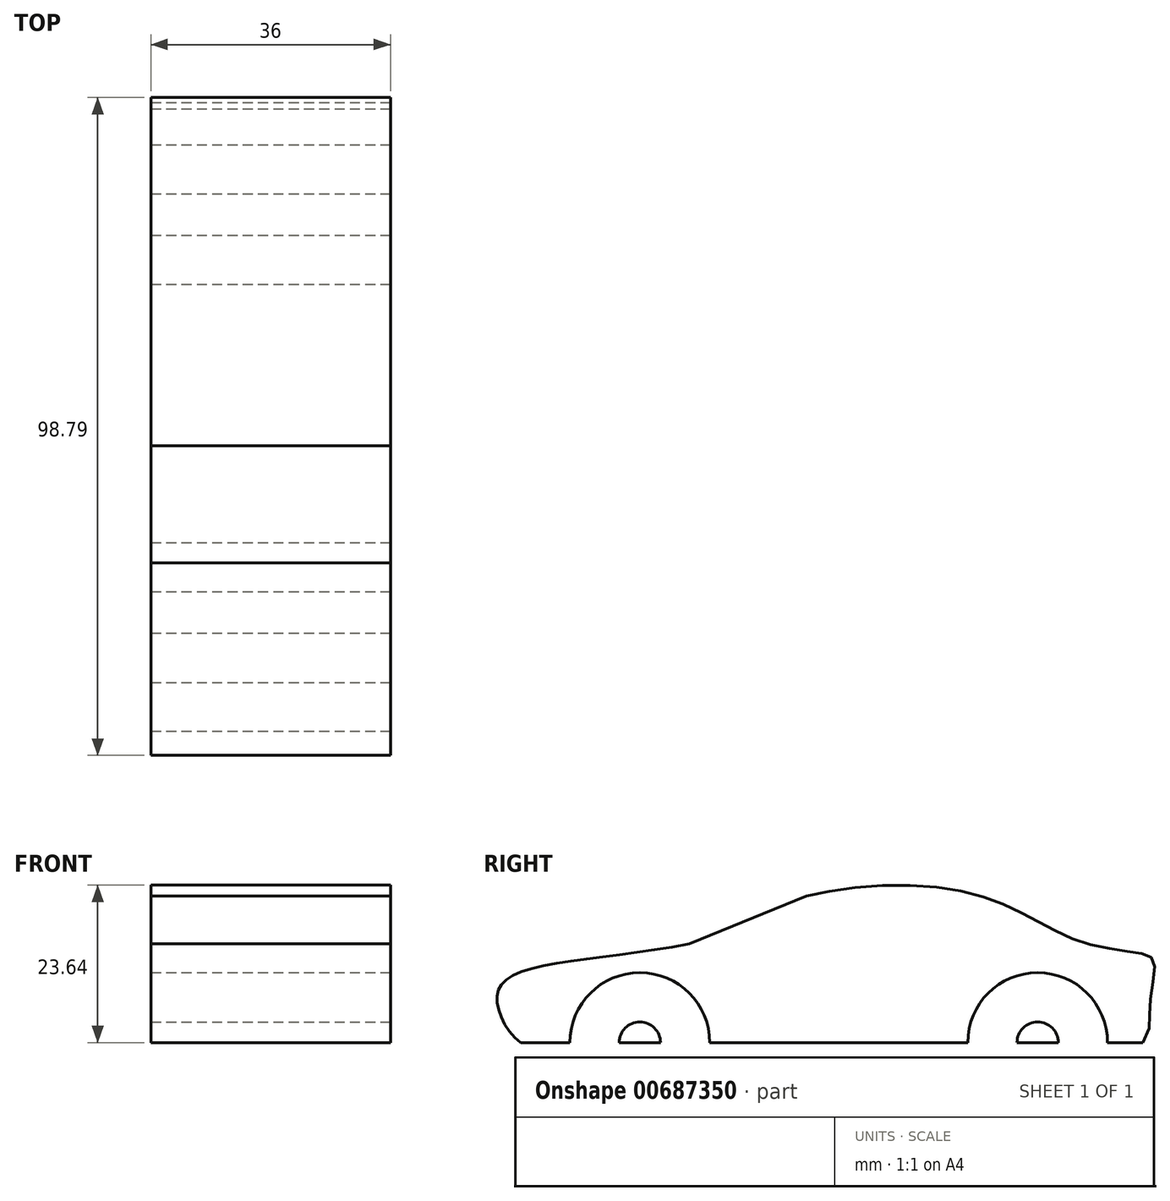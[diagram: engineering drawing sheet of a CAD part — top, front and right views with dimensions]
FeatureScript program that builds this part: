
annotation { "Feature Type Name" : "Feature", "Feature Type Description" : "" }
export const myFeature = defineFeature(function(context is Context, id is Id, definition is map)
    precondition{}
    {
        {
            var Q0;
            Q0=qCreatedBy(makeId("Right.planeOp"),FACE);
            var sketch = newSketch(context, id + "F0", { "sketchPlane" : qUnion([Q0])});
            skFitSpline(sketch, "E0", {"points": [v(0, 0) * mm, v(-17.92, 0) * mm], "startDerivative": vector(-17.92, 0) * mm, "endDerivative": vector(-17.92, 0) * mm});
            skFitSpline(sketch, "E1", {"points": [v(-17.92, 0) * mm, v(-21.44, 6.1) * mm, v(-19, 10.12) * mm, v(7.46, 14.82) * mm], "startDerivative": vector(-21.25, 15.42) * mm, "endDerivative": vector(59.63, 11.91) * mm});
            skLineSegment(sketch, "E2", {"start": v(7.46, 14.82) * mm, "end": v(25.02, 21.98) * mm});
            skFitSpline(sketch, "E3", {"points": [v(25.02, 21.98) * mm, v(43.8, 23.44) * mm, v(57.12, 19.62) * mm, v(66.03, 15.23) * mm, v(74.85, 13.45) * mm, v(77.2, 12.27) * mm, v(76.61, 5.61) * mm, v(75.56, 0) * mm], "startDerivative": vector(72.38, 18.5) * mm, "endDerivative": vector(-38.34, -51.68) * mm});
            skLineSegment(sketch, "E4", {"start": v(75.56, 0) * mm, "end": v(-5.97, 0) * mm});
            skSolve(sketch);
        }
        {
            var Q0;
            Q0 = qSketchRegion(id + "F0", true);
            extrude(context, id + "F1", {"entities" : qUnion([Q0]), "endBound" : BoundingType.SYMMETRIC, "depth" : 18 * 2 * mm, "offsetDistance" : 25 * mm});
        }
        {
            var Q0;
            Q0=makeQuery(id+"F1.opExtrude","CAP_FACE",FACE,{"disambiguationData":[OSD([sQuery(id+"F0.wireOp",EDGE,"E0"),sQuery(id+"F0.wireOp",EDGE,"E1"),sQuery(id+"F0.wireOp",EDGE,"E2"),sQuery(id+"F0.wireOp",EDGE,"E3"),sQuery(id+"F0.wireOp",EDGE,"E4")])],"isStart":false});
            var sketch = newSketch(context, id + "F2", { "sketchPlane" : qUnion([Q0])});
            skCircle(sketch, "E5", {"center": v(0, 0) * mm, "radius": 10.5 * mm});
            skLineSegment(sketch, "E6.bottom", {"start": v(0, -4.82) * mm, "end": v(5, -4.82) * mm});
            skLineSegment(sketch, "E6.top", {"start": v(0, 12.37) * mm, "end": v(5, 12.37) * mm});
            skLineSegment(sketch, "E6.left", {"start": v(0, -4.82) * mm, "end": v(0, 12.37) * mm});
            skLineSegment(sketch, "E6.right", {"start": v(5, -4.82) * mm, "end": v(5, 12.37) * mm});
            skLineSegment(sketch, "E7.MirrorCS", {"start": v(0, -4.82) * mm, "end": v(-5, -4.82) * mm});
            skLineSegment(sketch, "E8.MirrorCS", {"start": v(0, 12.37) * mm, "end": v(-5, 12.37) * mm});
            skLineSegment(sketch, "E9.MirrorCS", {"start": v(-5, -4.82) * mm, "end": v(-5, 12.37) * mm});
            skCircle(sketch, "E10", {"center": v(0, 0) * mm, "radius": 3.1 * mm});
            skCircle(sketch, "E11", {"center": v(59.77, 0) * mm, "radius": 10.5 * mm});
            skLineSegment(sketch, "E12.bottom", {"start": v(59.77, -4.82) * mm, "end": v(64.77, -4.82) * mm});
            skLineSegment(sketch, "E12.top", {"start": v(59.77, 12.37) * mm, "end": v(64.77, 12.37) * mm});
            skLineSegment(sketch, "E12.left", {"start": v(59.77, -4.82) * mm, "end": v(59.77, 12.37) * mm});
            skLineSegment(sketch, "E12.right", {"start": v(64.77, -4.82) * mm, "end": v(64.77, 12.37) * mm});
            skLineSegment(sketch, "E13.MirrorCS", {"start": v(59.77, -4.82) * mm, "end": v(54.77, -4.82) * mm});
            skLineSegment(sketch, "E14.MirrorCS", {"start": v(59.77, 12.37) * mm, "end": v(54.77, 12.37) * mm});
            skLineSegment(sketch, "E15.MirrorCS", {"start": v(54.77, -4.82) * mm, "end": v(54.77, 12.37) * mm});
            skCircle(sketch, "E16", {"center": v(59.77, 0) * mm, "radius": 3.1 * mm});
            skSolve(sketch);
        }
        {
            var Q0;
            {var subQ0=sQuery(id+"F2.wireOp",EDGE,"E7.MirrorCS");Q0=makeQuery(id+"F2.imprint","IMPRINT",FACE,{"disambiguationData":[TD([[makeQuery(id+"F2.imprint","IMPRINT",EDGE,{"derivedFrom":subQ0}),-1.0]])]});}
            var Q1;
            {var subQ6=sQuery(id+"F2.wireOp",EDGE,"E6.bottom");Q1=makeQuery(id+"F2.imprint","IMPRINT",FACE,{"disambiguationData":[TD([[makeQuery(id+"F2.imprint","IMPRINT",EDGE,{"derivedFrom":subQ6}),1.0]])]});}
            var Q2;
            {var subQ0=sQuery(id+"F2.wireOp",EDGE,"E13.MirrorCS");Q2=makeQuery(id+"F2.imprint","IMPRINT",FACE,{"disambiguationData":[TD([[makeQuery(id+"F2.imprint","IMPRINT",EDGE,{"derivedFrom":subQ0}),-1.0]])]});}
            var Q3;
            {var subQ6=sQuery(id+"F2.wireOp",EDGE,"E12.bottom");Q3=makeQuery(id+"F2.imprint","IMPRINT",FACE,{"disambiguationData":[TD([[makeQuery(id+"F2.imprint","IMPRINT",EDGE,{"derivedFrom":subQ6}),1.0]])]});}
            var Q4;
            Q4=makeQuery(id+"F1.opExtrude","CAP_FACE",FACE,{"disambiguationData":[OSD([sQuery(id+"F0.wireOp",EDGE,"E0"),sQuery(id+"F0.wireOp",EDGE,"E1"),sQuery(id+"F0.wireOp",EDGE,"E2"),sQuery(id+"F0.wireOp",EDGE,"E3"),sQuery(id+"F0.wireOp",EDGE,"E4")])],"isStart":true});
            extrude(context, id + "F3", {"entities" : qUnion([Q0, Q1, Q2, Q3]), "operationType" : NewBodyOperationType.ADD, "endBound" : BoundingType.UP_TO_SURFACE, "oppositeDirection" : true, "depth" : 25 * mm, "endBoundEntityFace" : qUnion([Q4]), "offsetDistance" : 25 * mm});
        }
        {
            var Q0;
            {var subQ0=sQuery(id+"F2.wireOp",EDGE,"E9.MirrorCS");var subQ1=sQuery(id+"F2.wireOp",EDGE,"E5");var subQ2=makeQuery(id+"F2.imprint","INTERSECT",VERTEX,{"derivedFrom":[subQ1,subQ0]});Q0=makeQuery(id+"F2.imprint","IMPRINT",FACE,{"disambiguationData":[TD([[makeQuery(id+"F2.imprint","IMPRINT",EDGE,{"disambiguationData":[TD([[subQ2,-1.0]])],"derivedFrom":subQ1}),1.0]])]});}
            var Q1;
            {var subQ0=sQuery(id+"F2.wireOp",EDGE,"E6.right");var subQ1=sQuery(id+"F2.wireOp",EDGE,"E5");var subQ2=makeQuery(id+"F2.imprint","INTERSECT",VERTEX,{"derivedFrom":[subQ1,subQ0]});Q1=makeQuery(id+"F2.imprint","IMPRINT",FACE,{"disambiguationData":[TD([[makeQuery(id+"F2.imprint","IMPRINT",EDGE,{"disambiguationData":[TD([[subQ2,1.0]])],"derivedFrom":subQ1}),1.0]])]});}
            var Q2;
            {var subQ0=sQuery(id+"F2.wireOp",EDGE,"E15.MirrorCS");var subQ1=sQuery(id+"F2.wireOp",EDGE,"E11");var subQ2=makeQuery(id+"F2.imprint","INTERSECT",VERTEX,{"derivedFrom":[subQ1,subQ0]});Q2=makeQuery(id+"F2.imprint","IMPRINT",FACE,{"disambiguationData":[TD([[makeQuery(id+"F2.imprint","IMPRINT",EDGE,{"disambiguationData":[TD([[subQ2,-1.0]])],"derivedFrom":subQ1}),1.0]])]});}
            var Q3;
            {var subQ0=sQuery(id+"F2.wireOp",EDGE,"E12.right");var subQ1=sQuery(id+"F2.wireOp",EDGE,"E11");var subQ2=makeQuery(id+"F2.imprint","INTERSECT",VERTEX,{"derivedFrom":[subQ1,subQ0]});Q3=makeQuery(id+"F2.imprint","IMPRINT",FACE,{"disambiguationData":[TD([[makeQuery(id+"F2.imprint","IMPRINT",EDGE,{"disambiguationData":[TD([[subQ2,1.0]])],"derivedFrom":subQ1}),1.0]])]});}
            extrude(context, id + "F4", {"entities" : qUnion([Q0, Q1, Q2, Q3]), "operationType" : NewBodyOperationType.REMOVE, "endBound" : BoundingType.THROUGH_ALL, "oppositeDirection" : true, "depth" : 25 * mm, "offsetDistance" : 25 * mm});
        }
        {
            var Q0;
            {var subQ0=sQuery(id+"F2.wireOp",EDGE,"E10");var subQ1=sQuery(id+"F2.wireOp",EDGE,"E6.left");var subQ2=makeQuery(id+"F2.imprint","INTERSECT",VERTEX,{"disambiguationData":[OD(1.0)],"derivedFrom":[subQ1,subQ0]});Q0=makeQuery(id+"F2.imprint","IMPRINT",FACE,{"disambiguationData":[TD([[makeQuery(id+"F2.imprint","IMPRINT",EDGE,{"disambiguationData":[TD([[subQ2,1.0]])],"derivedFrom":subQ1}),1.0]])]});}
            var Q1;
            {var subQ0=sQuery(id+"F2.wireOp",EDGE,"E10");var subQ1=sQuery(id+"F2.wireOp",EDGE,"E6.left");var subQ2=makeQuery(id+"F2.imprint","INTERSECT",VERTEX,{"disambiguationData":[OD(0.0)],"derivedFrom":[subQ1,subQ0]});Q1=makeQuery(id+"F2.imprint","IMPRINT",FACE,{"disambiguationData":[TD([[makeQuery(id+"F2.imprint","IMPRINT",EDGE,{"disambiguationData":[TD([[subQ2,-1.0]])],"derivedFrom":subQ1}),1.0]])]});}
            var Q2;
            {var subQ0=sQuery(id+"F2.wireOp",EDGE,"E10");var subQ1=sQuery(id+"F2.wireOp",EDGE,"E6.left");var subQ2=makeQuery(id+"F2.imprint","INTERSECT",VERTEX,{"disambiguationData":[OD(0.0)],"derivedFrom":[subQ1,subQ0]});Q2=makeQuery(id+"F2.imprint","IMPRINT",FACE,{"disambiguationData":[TD([[makeQuery(id+"F2.imprint","IMPRINT",EDGE,{"disambiguationData":[TD([[subQ2,-1.0]])],"derivedFrom":subQ1}),-1.0]])]});}
            var Q3;
            {var subQ0=sQuery(id+"F2.wireOp",EDGE,"E10");var subQ1=sQuery(id+"F2.wireOp",EDGE,"E6.left");var subQ2=makeQuery(id+"F2.imprint","INTERSECT",VERTEX,{"disambiguationData":[OD(1.0)],"derivedFrom":[subQ1,subQ0]});Q3=makeQuery(id+"F2.imprint","IMPRINT",FACE,{"disambiguationData":[TD([[makeQuery(id+"F2.imprint","IMPRINT",EDGE,{"disambiguationData":[TD([[subQ2,1.0]])],"derivedFrom":subQ1}),-1.0]])]});}
            var Q4;
            {var subQ0=sQuery(id+"F2.wireOp",EDGE,"E16");var subQ1=sQuery(id+"F2.wireOp",EDGE,"E12.left");var subQ2=makeQuery(id+"F2.imprint","INTERSECT",VERTEX,{"disambiguationData":[OD(1.0)],"derivedFrom":[subQ1,subQ0]});Q4=makeQuery(id+"F2.imprint","IMPRINT",FACE,{"disambiguationData":[TD([[makeQuery(id+"F2.imprint","IMPRINT",EDGE,{"disambiguationData":[TD([[subQ2,1.0]])],"derivedFrom":subQ1}),-1.0]])]});}
            var Q5;
            {var subQ0=sQuery(id+"F2.wireOp",EDGE,"E16");var subQ1=sQuery(id+"F2.wireOp",EDGE,"E12.left");var subQ2=makeQuery(id+"F2.imprint","INTERSECT",VERTEX,{"disambiguationData":[OD(1.0)],"derivedFrom":[subQ1,subQ0]});Q5=makeQuery(id+"F2.imprint","IMPRINT",FACE,{"disambiguationData":[TD([[makeQuery(id+"F2.imprint","IMPRINT",EDGE,{"disambiguationData":[TD([[subQ2,1.0]])],"derivedFrom":subQ1}),1.0]])]});}
            var Q6;
            {var subQ0=sQuery(id+"F2.wireOp",EDGE,"E16");var subQ1=sQuery(id+"F2.wireOp",EDGE,"E12.left");var subQ2=makeQuery(id+"F2.imprint","INTERSECT",VERTEX,{"disambiguationData":[OD(0.0)],"derivedFrom":[subQ1,subQ0]});Q6=makeQuery(id+"F2.imprint","IMPRINT",FACE,{"disambiguationData":[TD([[makeQuery(id+"F2.imprint","IMPRINT",EDGE,{"disambiguationData":[TD([[subQ2,-1.0]])],"derivedFrom":subQ1}),1.0]])]});}
            var Q7;
            {var subQ0=sQuery(id+"F2.wireOp",EDGE,"E16");var subQ1=sQuery(id+"F2.wireOp",EDGE,"E12.left");var subQ2=makeQuery(id+"F2.imprint","INTERSECT",VERTEX,{"disambiguationData":[OD(0.0)],"derivedFrom":[subQ1,subQ0]});Q7=makeQuery(id+"F2.imprint","IMPRINT",FACE,{"disambiguationData":[TD([[makeQuery(id+"F2.imprint","IMPRINT",EDGE,{"disambiguationData":[TD([[subQ2,-1.0]])],"derivedFrom":subQ1}),-1.0]])]});}
            extrude(context, id + "F5", {"entities" : qUnion([Q0, Q1, Q2, Q3, Q4, Q5, Q6, Q7]), "operationType" : NewBodyOperationType.REMOVE, "endBound" : BoundingType.THROUGH_ALL, "oppositeDirection" : true, "depth" : 25 * mm, "offsetDistance" : 25 * mm});
        }
        {
            var Q0;
            {var subQ1=sQuery(id+"F2.wireOp",EDGE,"E6.left");var subQ5=sQuery(id+"F2.wireOp",EDGE,"E5");var subQ6=makeQuery(id+"F2.imprint","INTERSECT",VERTEX,{"derivedFrom":[subQ5,subQ1]});Q0=makeQuery(id+"F2.imprint","IMPRINT",FACE,{"disambiguationData":[TD([[makeQuery(id+"F2.imprint","IMPRINT",EDGE,{"disambiguationData":[TD([[subQ6,-1.0]])],"derivedFrom":subQ5}),1.0]])]});}
            var Q1;
            {var subQ0=sQuery(id+"F2.wireOp",EDGE,"E6.right");var subQ1=sQuery(id+"F2.wireOp",EDGE,"E5");var subQ2=makeQuery(id+"F2.imprint","INTERSECT",VERTEX,{"derivedFrom":[subQ1,subQ0]});Q1=makeQuery(id+"F2.imprint","IMPRINT",FACE,{"disambiguationData":[TD([[makeQuery(id+"F2.imprint","IMPRINT",EDGE,{"disambiguationData":[TD([[subQ2,-1.0]])],"derivedFrom":subQ1}),1.0]])]});}
            var Q2;
            {var subQ6=sQuery(id+"F2.wireOp",EDGE,"E6.bottom");Q2=makeQuery(id+"F2.imprint","IMPRINT",FACE,{"disambiguationData":[TD([[makeQuery(id+"F2.imprint","IMPRINT",EDGE,{"derivedFrom":subQ6}),1.0]])]});}
            var Q3;
            {var subQ0=sQuery(id+"F2.wireOp",EDGE,"E7.MirrorCS");Q3=makeQuery(id+"F2.imprint","IMPRINT",FACE,{"disambiguationData":[TD([[makeQuery(id+"F2.imprint","IMPRINT",EDGE,{"derivedFrom":subQ0}),-1.0]])]});}
            var Q4;
            {var subQ0=sQuery(id+"F2.wireOp",EDGE,"E13.MirrorCS");Q4=makeQuery(id+"F2.imprint","IMPRINT",FACE,{"disambiguationData":[TD([[makeQuery(id+"F2.imprint","IMPRINT",EDGE,{"derivedFrom":subQ0}),-1.0]])]});}
            var Q5;
            {var subQ1=sQuery(id+"F2.wireOp",EDGE,"E12.left");var subQ5=sQuery(id+"F2.wireOp",EDGE,"E11");var subQ6=makeQuery(id+"F2.imprint","INTERSECT",VERTEX,{"derivedFrom":[subQ5,subQ1]});Q5=makeQuery(id+"F2.imprint","IMPRINT",FACE,{"disambiguationData":[TD([[makeQuery(id+"F2.imprint","IMPRINT",EDGE,{"disambiguationData":[TD([[subQ6,-1.0]])],"derivedFrom":subQ5}),1.0]])]});}
            var Q6;
            {var subQ0=sQuery(id+"F2.wireOp",EDGE,"E12.right");var subQ1=sQuery(id+"F2.wireOp",EDGE,"E11");var subQ2=makeQuery(id+"F2.imprint","INTERSECT",VERTEX,{"derivedFrom":[subQ1,subQ0]});Q6=makeQuery(id+"F2.imprint","IMPRINT",FACE,{"disambiguationData":[TD([[makeQuery(id+"F2.imprint","IMPRINT",EDGE,{"disambiguationData":[TD([[subQ2,-1.0]])],"derivedFrom":subQ1}),1.0]])]});}
            var Q7;
            {var subQ6=sQuery(id+"F2.wireOp",EDGE,"E12.bottom");Q7=makeQuery(id+"F2.imprint","IMPRINT",FACE,{"disambiguationData":[TD([[makeQuery(id+"F2.imprint","IMPRINT",EDGE,{"derivedFrom":subQ6}),1.0]])]});}
            extrude(context, id + "F6", {"entities" : qUnion([Q0, Q1, Q2, Q3, Q4, Q5, Q6, Q7]), "operationType" : NewBodyOperationType.REMOVE, "oppositeDirection" : true, "depth" : 9 * mm, "offsetDistance" : 25 * mm});
        }
    });
